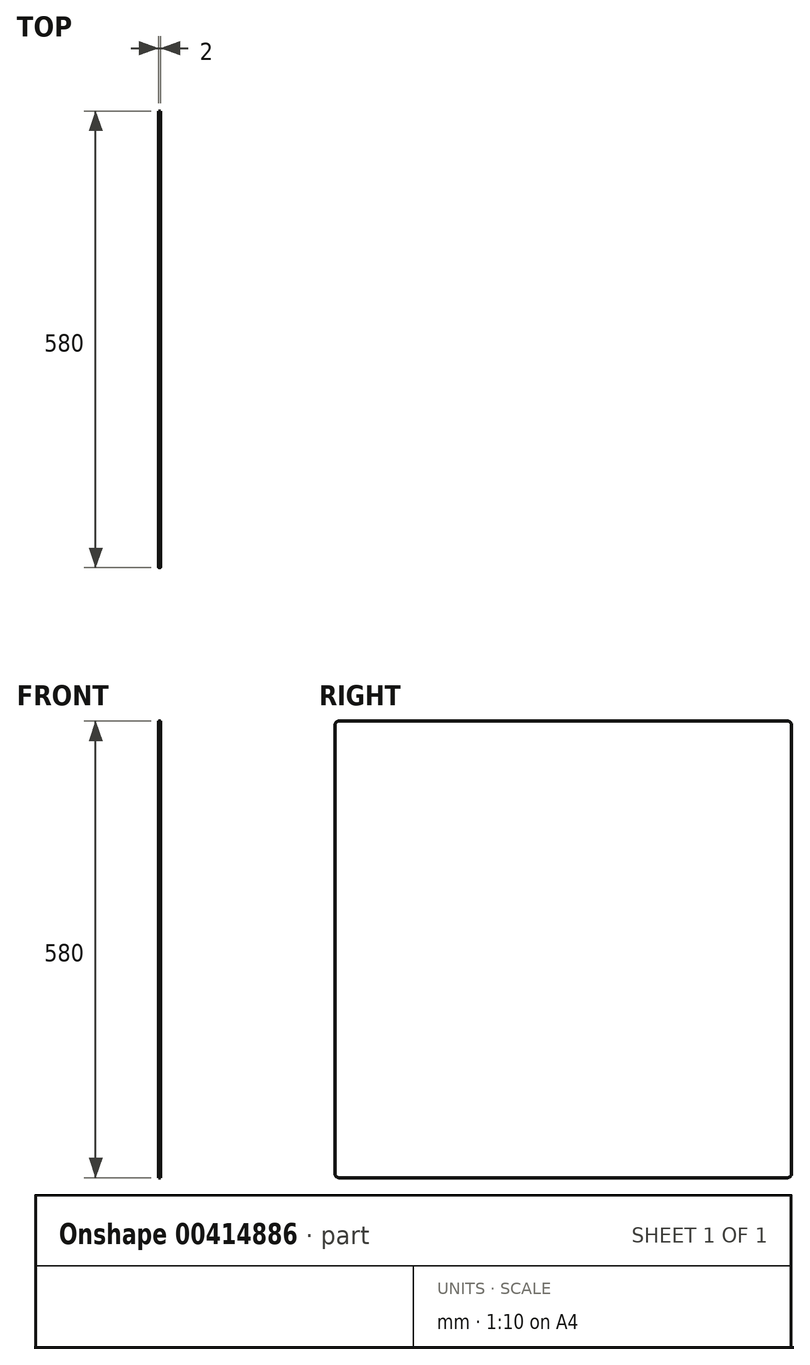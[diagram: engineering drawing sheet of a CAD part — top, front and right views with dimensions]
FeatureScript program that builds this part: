
annotation { "Feature Type Name" : "Feature", "Feature Type Description" : "" }
export const myFeature = defineFeature(function(context is Context, id is Id, definition is map)
    precondition{}
    {
        {
            var Q0;
            Q0=qCreatedBy(makeId("Right.planeOp"),FACE);
            var sketch = newSketch(context, id + "F0", { "sketchPlane" : qUnion([Q0])});
            skLineSegment(sketch, "E0.bottom", {"start": v(0, 0) * mm, "end": v(580, 0) * mm});
            skLineSegment(sketch, "E0.top", {"start": v(0, 580) * mm, "end": v(580, 580) * mm});
            skLineSegment(sketch, "E0.left", {"start": v(0, 0) * mm, "end": v(0, 580) * mm});
            skLineSegment(sketch, "E0.right", {"start": v(580, 0) * mm, "end": v(580, 580) * mm});
            skSolve(sketch);
        }
        {
            var Q0;
            Q0=makeQuery(id+"F0.imprint","IMPRINT",FACE,{"disambiguationData":[TD([[makeQuery(id+"F0.imprint","IMPRINT",EDGE,{"derivedFrom":sQuery(id+"F0.wireOp",EDGE,"E0.bottom")}),1.0]])]});
            extrude(context, id + "F1", {"entities" : qUnion([Q0]), "depth" : 2 * mm});
        }
        {
            var Q0;
            Q0=makeQuery(id+"F1.opExtrude","SWEPT_EDGE",EDGE,{"disambiguationData":[OSD([sQuery(id+"F0.wireOp",EDGE,"E0.top"),sQuery(id+"F0.wireOp",EDGE,"E0.left")])]});
            var Q1;
            Q1=makeQuery(id+"F1.opExtrude","SWEPT_EDGE",EDGE,{"disambiguationData":[OSD([sQuery(id+"F0.wireOp",EDGE,"E0.top"),sQuery(id+"F0.wireOp",EDGE,"E0.right")])]});
            var Q2;
            Q2=makeQuery(id+"F1.opExtrude","SWEPT_EDGE",EDGE,{"disambiguationData":[OSD([sQuery(id+"F0.wireOp",EDGE,"E0.bottom"),sQuery(id+"F0.wireOp",EDGE,"E0.right")])]});
            var Q3;
            Q3=makeQuery(id+"F1.opExtrude","SWEPT_EDGE",EDGE,{"disambiguationData":[OSD([sQuery(id+"F0.wireOp",EDGE,"E0.bottom"),sQuery(id+"F0.wireOp",EDGE,"E0.left")])]});
            fillet(context, id + "F2", {"entities" : qUnion([Q0, Q1, Q2, Q3]), "radius" : 5 * mm, "tangentPropagation" : true, "allowEdgeOverflow" : false});
        }
    });
